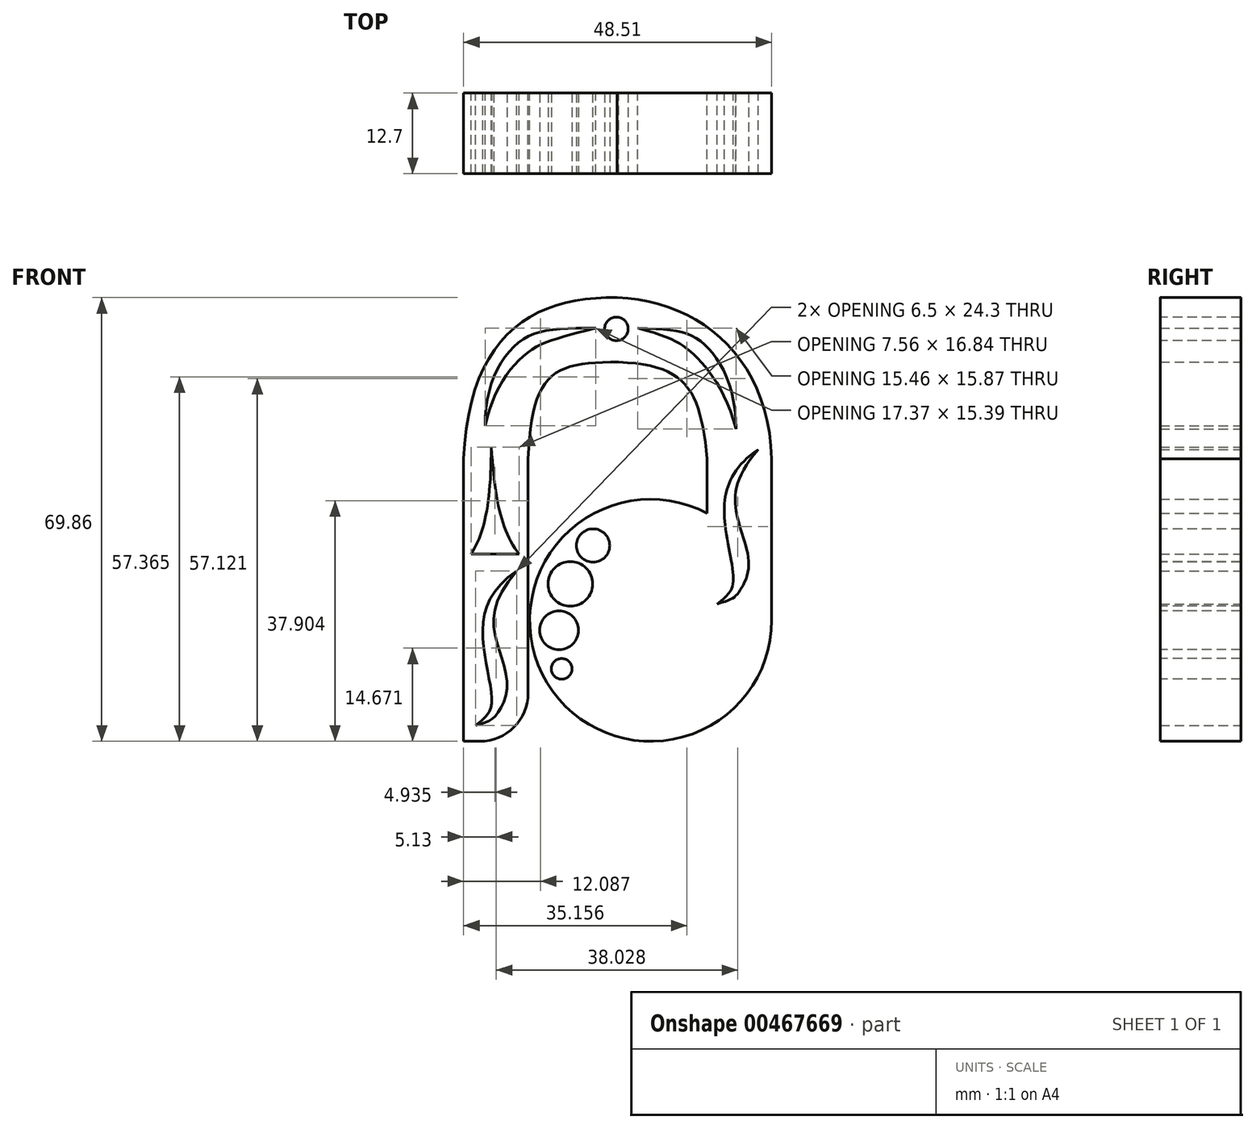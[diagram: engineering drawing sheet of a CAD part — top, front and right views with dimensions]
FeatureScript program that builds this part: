
annotation { "Feature Type Name" : "Feature", "Feature Type Description" : "" }
export const myFeature = defineFeature(function(context is Context, id is Id, definition is map)
    precondition{}
    {
        {
            var Q0;
            Q0=qCreatedBy(makeId("Front.planeOp"),FACE);
            var sketch = newSketch(context, id + "F0", { "sketchPlane" : qUnion([Q0])});
            skLineSegment(sketch, "E0", {"start": v(-47.4, -56.62) * mm, "end": v(-47.4, -12.17) * mm});
            skFitSpline(sketch, "E1", {"points": [v(-47.4, -12.17) * mm, v(-23.22, 13.23) * mm], "startDerivative": vector(2.46, 58.42) * mm, "endDerivative": vector(39.98, -0.86) * mm});
            skLineSegment(sketch, "E2.2", {"start": v(-37.24, -56.62) * mm, "end": v(-37.24, -12.17) * mm});
            skFitSpline(sketch, "E3", {"points": [v(-37.24, -12.17) * mm, v(-22.97, 3.07) * mm], "startDerivative": vector(1.6, 40.92) * mm, "endDerivative": vector(31.05, -0.35) * mm});
            skLineSegment(sketch, "E4", {"start": v(-47.4, -56.62) * mm, "end": v(-37.24, -56.62) * mm});
            skCircle(sketch, "E5", {"center": v(-17.94, -37.57) * mm, "radius": 19.05 * mm});
            skLineSegment(sketch, "E6", {"start": v(1.11, -37.57) * mm, "end": v(1.11, -12.17) * mm});
            skLineSegment(sketch, "E7.0", {"start": v(-9.05, -32.94) * mm, "end": v(-9.05, -12.17) * mm});
            skFitSpline(sketch, "E8", {"points": [v(1.11, -12.17) * mm, v(-23.22, 13.23) * mm], "startDerivative": vector(-1.62, 48.7) * mm, "endDerivative": vector(-38.57, 1.46) * mm});
            skFitSpline(sketch, "E9", {"points": [v(-22.97, 3.07) * mm, v(-9.05, -12.17) * mm], "startDerivative": vector(33.03, -1.16) * mm, "endDerivative": vector(3.26, -31.66) * mm});
            skLineSegment(sketch, "E10", {"start": v(-17.94, -37.57) * mm, "end": v(-17.94, -18.52) * mm});
            skLineSegment(sketch, "E11", {"start": v(-17.94, -37.57) * mm, "end": v(-17.94, -56.62) * mm});
            skLineSegment(sketch, "E12", {"start": v(-17.94, -37.57) * mm, "end": v(-36.99, -37.57) * mm});
            skFitSpline(sketch, "E13", {"points": [v(-43.05, -10.3) * mm, v(-46.25, -27.14) * mm], "startDerivative": vector(-0.12, -25.8) * mm, "endDerivative": vector(-6.6, -10.08) * mm});
            skFitSpline(sketch, "E14", {"points": [v(-43.05, -10.3) * mm, v(-38.69, -27.14) * mm], "startDerivative": vector(1.8, -25.56) * mm, "endDerivative": vector(8.4, -11.04) * mm});
            skLineSegment(sketch, "E15", {"start": v(-46.25, -27.14) * mm, "end": v(-38.69, -27.14) * mm});
            skFitSpline(sketch, "E16", {"points": [v(-44, -6.95) * mm, v(-38.9, 6.06) * mm, v(-26.63, 8.44) * mm], "startDerivative": vector(-0.97, 33.12) * mm, "endDerivative": vector(37.38, 0.1) * mm});
            skFitSpline(sketch, "E17", {"points": [v(-44, -6.95) * mm, v(-37.38, 4.54) * mm, v(-26.63, 8.44) * mm], "startDerivative": vector(6.46, 31.65) * mm, "endDerivative": vector(34.89, 9.52) * mm});
            skFitSpline(sketch, "E18", {"points": [v(-19.97, 8.44) * mm, v(-9.71, 6.06) * mm, v(-4.51, -7.44) * mm], "startDerivative": vector(35.98, -0.86) * mm, "endDerivative": vector(0.1, -37.38) * mm});
            skFitSpline(sketch, "E19", {"points": [v(-19.97, 8.44) * mm, v(-11.46, 4.54) * mm, v(-4.51, -7.44) * mm], "startDerivative": vector(32.61, -8.82) * mm, "endDerivative": vector(9.52, -34.89) * mm});
            skFitSpline(sketch, "E20", {"points": [v(-7.5, -34.99) * mm, v(-4.92, -30.87) * mm, v(-6.33, -21.41) * mm, v(-1, -10.68) * mm], "startDerivative": vector(25.18, 19.2) * mm, "endDerivative": vector(35.29, 23.5) * mm});
            skFitSpline(sketch, "E21", {"points": [v(-7.5, -34.99) * mm, v(-4.26, -33.38) * mm, v(-2.52, -29.05) * mm, v(-4.3, -21.3) * mm, v(-1, -10.68) * mm], "startDerivative": vector(34.07, 9.93) * mm, "endDerivative": vector(35.9, 41.24) * mm});
            skFitSpline(sketch, "E22", {"points": [v(-45.52, -54.1) * mm, v(-42.95, -49.98) * mm, v(-44.36, -40.53) * mm, v(-39.02, -29.8) * mm], "startDerivative": vector(25.18, 19.2) * mm, "endDerivative": vector(35.29, 23.5) * mm});
            skFitSpline(sketch, "E23", {"points": [v(-45.52, -54.1) * mm, v(-42.29, -52.5) * mm, v(-40.55, -48.16) * mm, v(-42.33, -40.42) * mm, v(-39.02, -29.8) * mm], "startDerivative": vector(34.07, 9.93) * mm, "endDerivative": vector(35.9, 41.24) * mm});
            skSolve(sketch);
        }
        {
            var Q0;
            Q0=makeQuery(id+"F0.imprint","IMPRINT",FACE,{"disambiguationData":[TD([[makeQuery(id+"F0.imprint","IMPRINT",EDGE,{"derivedFrom":sQuery(id+"F0.wireOp",EDGE,"E0")}),-1.0]])]});
            var Q1;
            {var subQ0=sQuery(id+"F0.wireOp",EDGE,"7ad8a8e8-3342-4443-83fd-cbfe6578de26.sketch_text.stroke-2");Q1=makeQuery(id+"F0.imprint","IMPRINT",FACE,{"disambiguationData":[TD([[makeQuery(id+"F0.imprint","IMPRINT",EDGE,{"derivedFrom":subQ0}),1.0]])]});}
            var Q2;
            {var subQ5=sQuery(id+"F0.wireOp",EDGE,"E5");var subQ7=sQuery(id+"F0.wireOp",EDGE,"E10");var subQ8=makeQuery(id+"F0.imprint","INTERSECT",VERTEX,{"derivedFrom":[subQ5,subQ7]});Q2=makeQuery(id+"F0.imprint","IMPRINT",FACE,{"disambiguationData":[TD([[makeQuery(id+"F0.imprint","IMPRINT",EDGE,{"disambiguationData":[TD([[subQ8,-1.0]])],"derivedFrom":subQ5}),1.0]])]});}
            var Q3;
            {var subQ11=sQuery(id+"F0.wireOp",EDGE,"7ad8a8e8-3342-4443-83fd-cbfe6578de26.sketch_text.stroke-0");Q3=makeQuery(id+"F0.imprint","IMPRINT",FACE,{"disambiguationData":[TD([[makeQuery(id+"F0.imprint","IMPRINT",EDGE,{"derivedFrom":subQ11}),1.0]])]});}
            var Q4;
            {var subQ3=sQuery(id+"F0.wireOp",EDGE,"E10");Q4=makeQuery(id+"F0.imprint","IMPRINT",FACE,{"disambiguationData":[TD([[makeQuery(id+"F0.imprint","IMPRINT",EDGE,{"derivedFrom":subQ3}),-1.0]])]});}
            var Q5;
            {var subQ0=sQuery(id+"F0.wireOp",EDGE,"E11");Q5=makeQuery(id+"F0.imprint","IMPRINT",FACE,{"disambiguationData":[TD([[makeQuery(id+"F0.imprint","IMPRINT",EDGE,{"derivedFrom":subQ0}),-1.0]])]});}
            extrude(context, id + "F1", {"entities" : qUnion([Q0, Q1, Q2, Q3, Q4, Q5]), "endBound" : BoundingType.SYMMETRIC, "depth" : 12.7 * mm, "offsetDistance" : 25.4 * mm});
        }
        {
            var Q0;
            Q0=makeQuery(id+"F1.opExtrude","SWEPT_EDGE",EDGE,{"disambiguationData":[OSD([sQuery(id+"F0.wireOp",EDGE,"E2.2"),sQuery(id+"F0.wireOp",EDGE,"E4")])]});
            fillet(context, id + "F2", {"entities" : qUnion([Q0]), "radius" : 7.62 * mm, "tangentPropagation" : true, "allowEdgeOverflow" : false});
        }
        {
            var Q0;
            Q0=qCreatedBy(makeId("Front.planeOp"),FACE);
            var sketch = newSketch(context, id + "F3", { "sketchPlane" : qUnion([Q0])});
            skCircle(sketch, "E24", {"center": v(-23.35, 8.32) * mm, "radius": 1.85 * mm});
            skCircle(sketch, "E25", {"center": v(-27.03, -25.8) * mm, "radius": 2.62 * mm});
            skCircle(sketch, "E26", {"center": v(-30.6, -31.83) * mm, "radius": 3.5 * mm});
            skCircle(sketch, "E27", {"center": v(-32.37, -39.13) * mm, "radius": 3.06 * mm});
            skCircle(sketch, "E28", {"center": v(-31.96, -45.2) * mm, "radius": 1.62 * mm});
            skSolve(sketch);
        }
        {
            var Q0;
            Q0 = qSketchRegion(id + "F3", true);
            extrude(context, id + "F4", {"entities" : qUnion([Q0]), "operationType" : NewBodyOperationType.REMOVE, "endBound" : BoundingType.SYMMETRIC, "oppositeDirection" : true, "depth" : 25.4 * mm});
        }
    });
